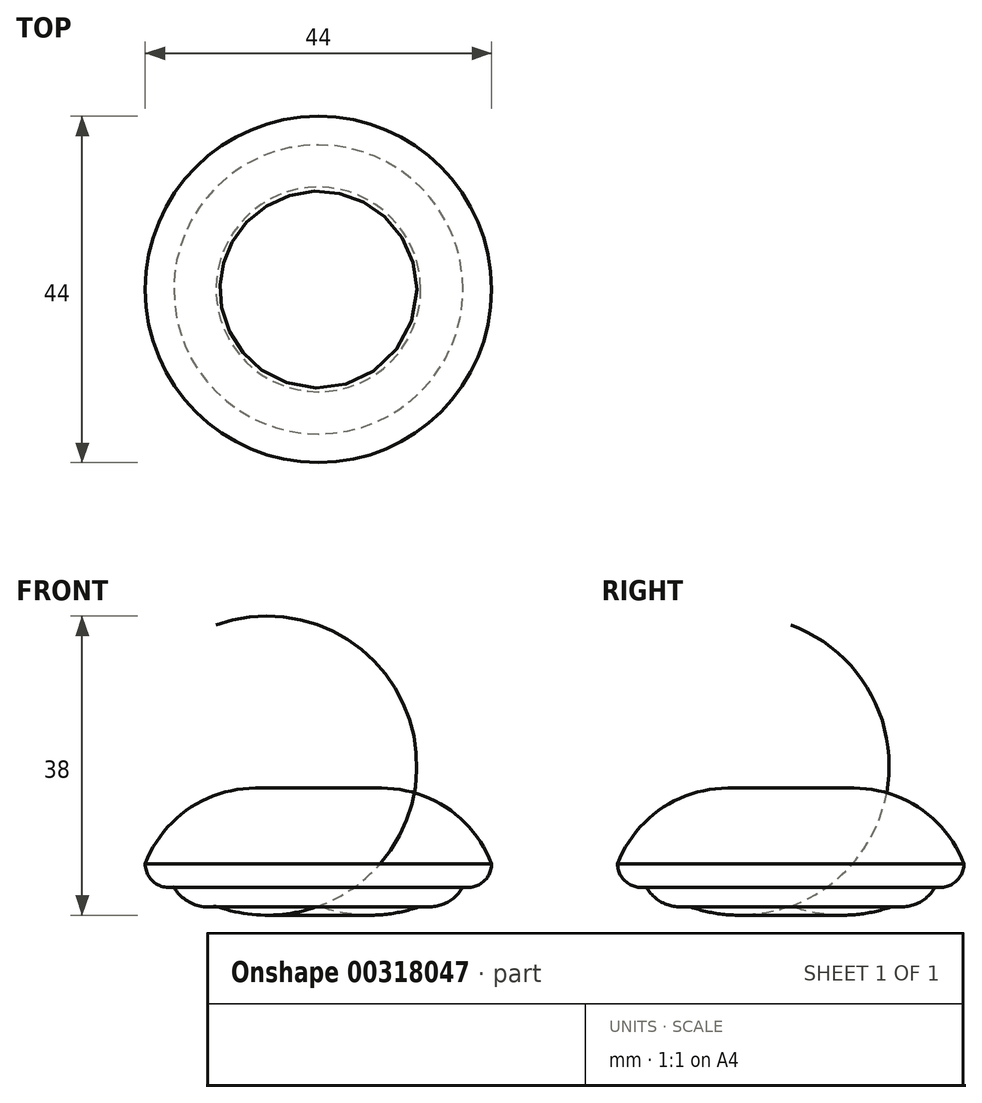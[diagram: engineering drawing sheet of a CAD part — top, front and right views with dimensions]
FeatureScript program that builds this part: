
annotation { "Feature Type Name" : "Feature", "Feature Type Description" : "" }
export const myFeature = defineFeature(function(context is Context, id is Id, definition is map)
    precondition{}
    {
        {
            var Q0;
            Q0=qCreatedBy(makeId("Front.planeOp"),FACE);
            var sketch = newSketch(context, id + "F0", { "sketchPlane" : qUnion([Q0])});
            skLineSegment(sketch, "E0", {"start": v(0, 0) * mm, "end": v(8, 0) * mm});
            skArc(sketch, "E1", {"start": v(22, -9.61) * mm, "mid": v(16.5, -2.64) * mm, "end": v(8, 0) * mm});
            skArc(sketch, "E2", {"start": v(18.36, -12.55) * mm, "mid": v(20.88, -11.95) * mm, "end": v(22, -9.61) * mm});
            skLineSegment(sketch, "E3", {"start": v(18.36, -12.55) * mm, "end": v(0.36, -12.55) * mm});
            skArc(sketch, "E4", {"start": v(13, -15) * mm, "mid": v(16.08, -14.65) * mm, "end": v(18.36, -12.55) * mm});
            skLineSegment(sketch, "E5", {"start": v(13, -15) * mm, "end": v(0, -15) * mm});
            skArc(sketch, "E6", {"start": v(0, -15) * mm, "mid": v(6.5, -16.15) * mm, "end": v(13, -15) * mm});
            skLineSegment(sketch, "E7", {"start": v(0, -15) * mm, "end": v(0, 0) * mm});
            skSolve(sketch);
        }
        {
            var Q0;
            Q0 = qSketchRegion(id + "F0", true);
            var Q1;
            Q1=sQuery(id+"F0.wireOp",EDGE,"E7");
            revolve(context, id + "F1", {"entities" : qUnion([Q0]), "axis" : qUnion([Q1]), "revolveType" : RevolveType.FULL});
        }
    });
